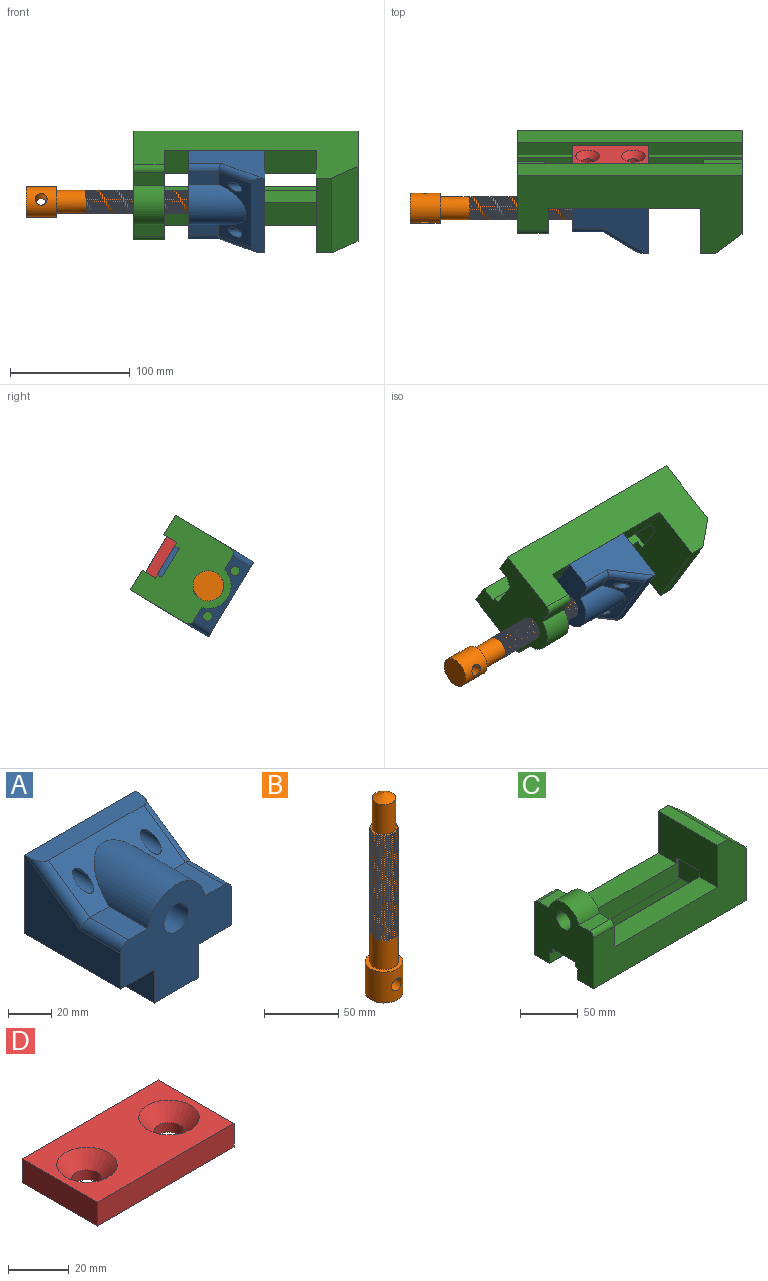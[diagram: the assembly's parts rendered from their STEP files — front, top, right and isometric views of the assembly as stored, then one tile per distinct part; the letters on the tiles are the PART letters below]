
ASSEMBLY  parts=4 mates=3
PART A: 26 faces, bbox 73x63.5x67.7 mm
  f0: plane 73.03x10.89mm, normal (0,0,1), area 776.2mm2, adj f1,f2,f9,f13,f22,f24
  f1: plane 63.5x44.45mm, normal (-1,0,0), area 1755.2mm2, adj f0,f3,f8,f9,f24,f25
  f2: plane 63.5x44.45mm, normal (1,0,0), area 1755.2mm2, adj f0,f7,f8,f9,f22,f23
  f3: plane 63.5x22.23mm, normal (0,0,-1), area 1411.3mm2, adj f1,f4,f8,f9
  f4: plane 63.5x19.05mm, normal (-1,0,0), area 1209.7mm2, adj f3,f5,f8,f9
  f5: plane 63.5x28.58mm, normal (0,0,-1), area 1715.5mm2, adj f4,f6,f8,f9,f19,f21
  f6: plane 63.5x19.05mm, normal (1,0,0), area 1209.7mm2, adj f5,f7,f8,f9
  f7: plane 63.5x22.23mm, normal (0,0,-1), area 1411.3mm2, adj f2,f6,f8,f9
  f8: plane 73.03x60.33mm, normal (0,-1,0), area 2639.8mm2, adj f1,f2,f3,f4,f5,f6,f7,f10
  f9: plane 73.03x63.5mm, normal (0,1,0), area 3691.3mm2, adj f0,f1,f2,f3,f4,f5,f6,f7
  f10: cylinder r=19.05mm len=48.15mm, axis (0,-1,0), area 2137.7mm2, adj f8,f11,f12,f13
  f11: plane 25.4x12.65mm, normal (0,0,1), area 321.3mm2, adj f8,f10,f13,f23
  f12: plane 25.4x12.65mm, normal (0,0,1), area 321.3mm2, adj f8,f10,f13,f25
  f13: plane 62.87x27.21mm, normal (0,-0.57,0.82), area 1131.4mm2, adj f0,f10,f11,f12,f16,f17,f22,f24
  f14: cone r=0mm half-angle=59deg, axis (0,-1,0), area 230.9mm2, adj f15
  f15: cylinder r=7.94mm len=53.34mm, axis (0,-1,0), area 2660.2mm2, adj f8,f14
  f16: cylinder r=3.97mm len=30.24mm, axis (0,1,0), area 610.9mm2, adj f9,f13
  f17: cylinder r=3.97mm len=30.24mm, axis (0,1,0), area 610.9mm2, adj f9,f13
  f18: cone r=0mm half-angle=59deg, axis (0,0,-1), area 57.7mm2, adj f19
  f19: cylinder r=3.97mm len=28.58mm, axis (0,0,-1), area 712.6mm2, adj f5,f18
  f20: cone r=0mm half-angle=59deg, axis (0,0,-1), area 57.7mm2, adj f21
  f21: cylinder r=3.97mm len=28.58mm, axis (0,0,-1), area 712.6mm2, adj f5,f20
  f22: cylinder r=5.08mm len=37.38mm, axis (0,-0.82,-0.57), area 290.7mm2, adj f0,f2,f13,f23
  f23: cylinder r=5.08mm len=27mm, axis (0,1,0), area 207.3mm2, adj f2,f8,f11,f22
  f24: cylinder r=5.08mm len=37.38mm, axis (0,0.82,0.57), area 290.7mm2, adj f0,f1,f13,f25
  f25: cylinder r=5.08mm len=27mm, axis (0,1,0), area 207.3mm2, adj f1,f8,f12,f24
PART B: 65 faces, bbox 25.7x25.7x165.1 mm
  f0: cylinder r=12.7mm len=25.4mm, axis (0,0,-1), area 1872.6mm2, adj f59,f60,f64
  f1: cylinder r=9.53mm len=26.74mm, axis (0,0,-1), area 1515.1mm2, adj f54,f59,f61,f62,f63
  f2: cylinder r=9.53mm len=19.05mm, axis (0,0,-1), area 50mm2, adj f3,f55,f56,f62,f63
  f3: cylinder r=9.53mm len=19.05mm, axis (0,0,-1), area 56.2mm2, adj f2,f4,f62,f63
  f4: cylinder r=9.53mm len=19.05mm, axis (0,0,-1), area 56.3mm2, adj f3,f5,f62,f63
  f5: cylinder r=9.53mm len=19.05mm, axis (0,0,-1), area 56.3mm2, adj f4,f6,f62,f63
  f6: cylinder r=9.53mm len=19.05mm, axis (0,0,-1), area 56.3mm2, adj f5,f7,f62,f63
  f7: cylinder r=9.53mm len=19.05mm, axis (0,0,-1), area 56.2mm2, adj f6,f8,f62,f63
  f8: cylinder r=9.53mm len=19.05mm, axis (0,0,-1), area 56.2mm2, adj f7,f9,f62,f63
  f9: cylinder r=9.53mm len=19.05mm, axis (0,0,-1), area 56.3mm2, adj f8,f10,f62,f63
  f10: cylinder r=9.53mm len=19.05mm, axis (0,0,-1), area 56.2mm2, adj f9,f11,f62,f63
  f11: cylinder r=9.53mm len=19.05mm, axis (0,0,-1), area 56.2mm2, adj f10,f12,f62,f63
  f12: cylinder r=9.53mm len=19.05mm, axis (0,0,-1), area 56.3mm2, adj f11,f13,f62,f63
  f13: cylinder r=9.53mm len=19.05mm, axis (0,0,-1), area 56.3mm2, adj f12,f14,f62,f63
  f14: cylinder r=9.53mm len=19.05mm, axis (0,0,-1), area 56.2mm2, adj f13,f15,f62,f63
  f15: cylinder r=9.53mm len=19.05mm, axis (0,0,-1), area 56.2mm2, adj f14,f16,f62,f63
  f16: cylinder r=9.53mm len=19.05mm, axis (0,0,-1), area 56.2mm2, adj f15,f17,f62,f63
  f17: cylinder r=9.53mm len=19.05mm, axis (0,0,-1), area 56.3mm2, adj f16,f18,f62,f63
  f18: cylinder r=9.53mm len=19.05mm, axis (0,0,-1), area 56.2mm2, adj f17,f19,f62,f63
  f19: cylinder r=9.53mm len=19.05mm, axis (0,0,-1), area 56.3mm2, adj f18,f20,f62,f63
  f20: cylinder r=9.53mm len=19.05mm, axis (0,0,-1), area 56.3mm2, adj f19,f21,f62,f63
  f21: cylinder r=9.53mm len=19.05mm, axis (0,0,-1), area 56.3mm2, adj f20,f22,f62,f63
  f22: cylinder r=9.53mm len=19.05mm, axis (0,0,-1), area 56.2mm2, adj f21,f23,f62,f63
  f23: cylinder r=9.53mm len=19.05mm, axis (0,0,-1), area 56.2mm2, adj f22,f24,f62,f63
  f24: cylinder r=9.53mm len=19.05mm, axis (0,0,-1), area 56.3mm2, adj f23,f25,f62,f63
  f25: cylinder r=9.53mm len=19.05mm, axis (0,0,-1), area 56.2mm2, adj f24,f26,f62,f63
  f26: cylinder r=9.53mm len=19.05mm, axis (0,0,-1), area 56.2mm2, adj f25,f27,f62,f63
  f27: cylinder r=9.53mm len=19.05mm, axis (0,0,-1), area 56.3mm2, adj f26,f28,f62,f63
  f28: cylinder r=9.53mm len=19.05mm, axis (0,0,-1), area 56.3mm2, adj f27,f29,f62,f63
  f29: cylinder r=9.53mm len=19.05mm, axis (0,0,-1), area 56.3mm2, adj f28,f30,f62,f63
  f30: cylinder r=9.53mm len=19.05mm, axis (0,0,-1), area 56.2mm2, adj f29,f31,f62,f63
  f31: cylinder r=9.53mm len=19.05mm, axis (0,0,-1), area 56.2mm2, adj f30,f32,f62,f63
  f32: cylinder r=9.53mm len=19.05mm, axis (0,0,-1), area 56.3mm2, adj f31,f33,f62,f63
  f33: cylinder r=9.53mm len=19.05mm, axis (0,0,-1), area 56.2mm2, adj f32,f34,f62,f63
  f34: cylinder r=9.53mm len=19.05mm, axis (0,0,-1), area 56.2mm2, adj f33,f35,f62,f63
  f35: cylinder r=9.53mm len=19.05mm, axis (0,0,-1), area 56.3mm2, adj f34,f36,f62,f63
  f36: cylinder r=9.53mm len=19.05mm, axis (0,0,-1), area 56.3mm2, adj f35,f37,f62,f63
  f37: cylinder r=9.53mm len=19.05mm, axis (0,0,-1), area 56.3mm2, adj f36,f38,f62,f63
  f38: cylinder r=9.53mm len=19.05mm, axis (0,0,-1), area 56.2mm2, adj f37,f39,f62,f63
  f39: cylinder r=9.53mm len=19.05mm, axis (0,0,-1), area 56.3mm2, adj f38,f40,f62,f63
  f40: cylinder r=9.53mm len=19.05mm, axis (0,0,-1), area 56.2mm2, adj f39,f41,f62,f63
  f41: cylinder r=9.53mm len=19.05mm, axis (0,0,-1), area 56.2mm2, adj f40,f42,f62,f63
  f42: cylinder r=9.53mm len=19.05mm, axis (0,0,-1), area 56.3mm2, adj f41,f43,f62,f63
  f43: cylinder r=9.53mm len=19.05mm, axis (0,0,-1), area 56.3mm2, adj f42,f44,f62,f63
  f44: cylinder r=9.53mm len=19.05mm, axis (0,0,-1), area 56.3mm2, adj f43,f45,f62,f63
  f45: cylinder r=9.53mm len=19.05mm, axis (0,0,-1), area 56.2mm2, adj f44,f46,f62,f63
  f46: cylinder r=9.53mm len=19.05mm, axis (0,0,-1), area 56.2mm2, adj f45,f47,f62,f63
  f47: cylinder r=9.53mm len=19.05mm, axis (0,0,-1), area 56.3mm2, adj f46,f48,f62,f63
  f48: cylinder r=9.53mm len=19.05mm, axis (0,0,-1), area 56.2mm2, adj f47,f49,f62,f63
  f49: cylinder r=9.53mm len=19.05mm, axis (0,0,-1), area 56.2mm2, adj f48,f50,f62,f63
  f50: cylinder r=9.53mm len=19.05mm, axis (0,0,-1), area 56.3mm2, adj f49,f51,f62,f63
  f51: cylinder r=9.53mm len=19.05mm, axis (0,0,-1), area 56.3mm2, adj f50,f52,f62,f63
  f52: cylinder r=9.53mm len=19.05mm, axis (0,0,-1), area 56.3mm2, adj f51,f53,f62,f63
  f53: cylinder r=9.53mm len=19.05mm, axis (0,0,-1), area 56.2mm2, adj f52,f54,f62,f63
  f54: cylinder r=9.53mm len=19.05mm, axis (0,0,-1), area 56.3mm2, adj f1,f53,f62,f63
  f55: cylinder r=9.53mm len=9.43mm, axis (0,0,-1), area 2.5mm2, adj f2,f56,f63
  f56: plane 19.34x19.02mm, normal (0,0,1), area 80.4mm2, adj f2,f55,f58,f62,f63
  f57: cone r=0mm half-angle=60deg, axis (0,0,-1), area 228.6mm2, adj f58
  f58: cylinder r=7.94mm len=24.52mm, axis (0,0,-1), area 1222.9mm2, adj f56,f57
  f59: plane 25.4x25.4mm, normal (0,0,1), area 221.7mm2, adj f0,f1
  f60: plane 25.4x25.4mm, normal (0,0,-1), area 506.7mm2, adj f0
  f61: plane 0.65x0.56mm, normal (0.11,-0.99,0), area 0.2mm2, adj f1,f62,f63
  f62: bspline ~87.54x23.79mm, area 2031.3mm2, adj f1,f2,f3,f4,f5,f6,f7,f8
  f63: bspline ~87.31x23.79mm, area 2047.8mm2, adj f1,f2,f3,f4,f5,f6,f7,f8
  f64: cylinder r=4.9mm len=25.4mm, axis (0,1,0), area 782.4mm2, adj f0
PART C: 30 faces, bbox 187.3x73x76.2 mm
  f0: plane 28.58x3.18mm, normal (0,0,-1), area 90.7mm2, adj f1,f2,f16,f27
  f1: plane 187.33x25.4mm, normal (0,-1,0), area 2766.5mm2, adj f0,f2,f6,f7,f9,f12,f14,f15
  f2: plane 73.03x41.28mm, normal (1,0,0), area 1929.2mm2, adj f0,f1,f3,f4,f6,f13,f16,f20
  f3: plane 187.33x76.2mm, normal (0,1,0), area 7844.7mm2, adj f2,f5,f6,f7,f9,f10,f11,f12
  f4: plane 187.33x76.2mm, normal (0,-1,0), area 7844.7mm2, adj f2,f7,f8,f9,f10,f11,f12,f13
  f5: plane 187.33x19.05mm, normal (0,0,-1), area 3568.5mm2, adj f3,f7,f9,f19
  f6: plane 127x22.21mm, normal (0,0,1), area 2821mm2, adj f1,f2,f3,f12
  f7: plane 73.03x73.03mm, normal (-1,0,0), area 3859mm2, adj f1,f3,f4,f5,f8,f14,f16,f17
  f8: plane 187.33x19.05mm, normal (0,0,-1), area 3568.5mm2, adj f4,f7,f9,f18
  f9: plane 73.03x57.15mm, normal (1,0,0), area 3651.2mm2, adj f1,f3,f4,f5,f8,f10,f14,f16
  f10: plane 73.03x22.23mm, normal (0.65,0,0.76), area 2137.6mm2, adj f3,f4,f9,f11
  f11: plane 73.03x12.7mm, normal (0,0,1), area 927.4mm2, adj f3,f4,f10,f12
  f12: plane 73.03x44.45mm, normal (-1,0,0), area 3064.5mm2, adj f1,f3,f4,f6,f11,f13,f15,f16
  f13: plane 127x22.24mm, normal (0,0,1), area 2824.2mm2, adj f2,f4,f12,f16
  f14: plane 187.33x3.16mm, normal (0,0,-1), area 592.4mm2, adj f1,f7,f9,f19
  f15: plane 28.58x3.18mm, normal (0,0,-1), area 90.7mm2, adj f1,f12,f16,f25
  f16: plane 187.33x25.4mm, normal (0,1,0), area 2766.5mm2, adj f0,f2,f7,f9,f12,f13,f15,f17
  f17: plane 187.33x3.19mm, normal (0,0,-1), area 597.1mm2, adj f7,f9,f16,f18
  f18: plane 187.33x12.7mm, normal (0,1,0), area 2379mm2, adj f7,f8,f9,f17
  f19: plane 187.33x12.7mm, normal (0,-1,0), area 2379mm2, adj f5,f7,f9,f14
  f20: cylinder r=19.05mm len=36.89mm, axis (-1,0,0), area 1275.6mm2, adj f2,f7,f21,f22
  f21: plane 25.4x12.99mm, normal (0,0,1), area 329.9mm2, adj f2,f7,f20,f29
  f22: plane 25.4x12.99mm, normal (0,0,1), area 329.9mm2, adj f2,f7,f20,f28
  f23: cylinder r=8.73mm len=25.4mm, axis (-1,0,0), area 1393.4mm2, adj f2,f7
  f24: plane 31.75x28.58mm, normal (0,0,-1), area 907.3mm2, adj f1,f9,f16,f25
  f25: plane 28.58x22.65mm, normal (-1,0,0), area 647.2mm2, adj f1,f15,f16,f24
  f26: plane 28.58x22.23mm, normal (0,0,-1), area 635.1mm2, adj f1,f7,f16,f27
  f27: plane 28.58x20.97mm, normal (1,0,0), area 599.2mm2, adj f0,f1,f16,f26
  f28: cylinder r=5.08mm len=25.4mm, axis (-1,0,0), area 202.7mm2, adj f2,f3,f7,f22
  f29: cylinder r=5.08mm len=25.4mm, axis (1,0,0), area 202.7mm2, adj f2,f4,f7,f21
PART D: 10 faces, bbox 63.5x34.9x9.5 mm
  f0: plane 34.93x9.53mm, normal (-1,0,0), area 332.7mm2, adj f1,f3,f4,f5
  f1: plane 63.5x9.53mm, normal (0,-1,0), area 604.8mm2, adj f0,f2,f4,f5
  f2: plane 34.93x9.53mm, normal (1,0,0), area 332.7mm2, adj f1,f3,f4,f5
  f3: plane 63.5x9.53mm, normal (0,1,0), area 604.8mm2, adj f0,f2,f4,f5
  f4: plane 63.5x34.93mm, normal (0,0,1), area 1599.6mm2, adj f0,f1,f2,f3,f7,f9
  f5: plane 63.5x34.93mm, normal (0,0,-1), area 2058mm2, adj f0,f1,f2,f3,f6,f8
  f6: cylinder r=5.04mm len=10.08mm, axis (0,0,1), area 124mm2, adj f5,f7
  f7: cone r=5.04mm half-angle=41deg, axis (0,0,1), area 349.4mm2, adj f4,f6
  f8: cylinder r=5.04mm len=10.08mm, axis (0,0,1), area 124mm2, adj f5,f9
  f9: cone r=5.04mm half-angle=41deg, axis (0,0,1), area 349.4mm2, adj f4,f8
PLACE A rot(axis=(0.66,0.66,-0.37),139.3deg) t=(-38.38,120.2,-44.39)mm
PLACE B rot(axis=(0.71,0.06,0.71),172.9deg) t=(-72.81,90.31,-62.44)mm
PLACE C rot(axis=(1,0,0),121.1deg) t=(39.69,136.52,-34.56)mm
PLACE D rot(axis=(-1,0,0),58.9deg) t=(-70.13,125.64,-41.11)mm
MATE cylindrical B.f1 <-> C.f20  axis (-1,0,0) through (-72.81,90.31,-62.44)mm
MATE slider A.f8 <-> C.f2  axis (-1,0,0) through (-101.88,101.95,-38.72)mm
MATE fastened D.f6 <-> A.f18  axis (0,-0.86,-0.52) through (-89.18,125.64,-41.11)mm
